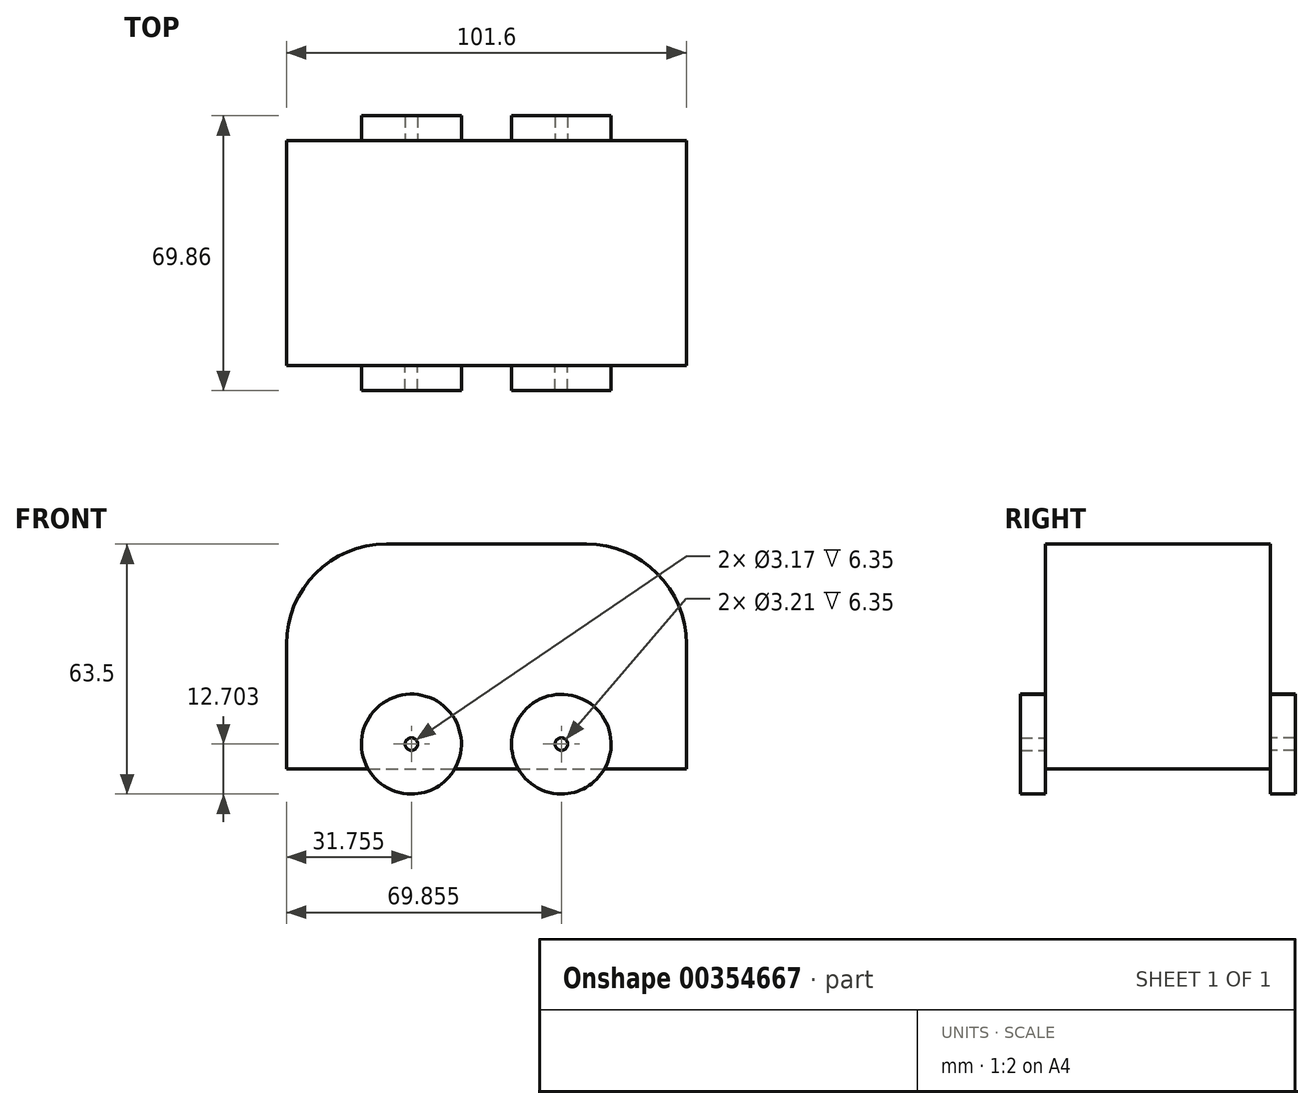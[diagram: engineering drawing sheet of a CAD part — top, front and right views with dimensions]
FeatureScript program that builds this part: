
annotation { "Feature Type Name" : "Feature", "Feature Type Description" : "" }
export const myFeature = defineFeature(function(context is Context, id is Id, definition is map)
    precondition{}
    {
        {
            var Q0;
            Q0=qCreatedBy(makeId("Front.planeOp"),FACE);
            var sketch = newSketch(context, id + "F0", { "sketchPlane" : qUnion([Q0])});
            skLineSegment(sketch, "E0.bottom", {"start": v(-26.04, 40.52) * mm, "end": v(24.77, 40.52) * mm});
            skLineSegment(sketch, "E0.top", {"start": v(-51.44, -16.63) * mm, "end": v(50.16, -16.63) * mm});
            skLineSegment(sketch, "E0.left", {"start": v(-51.44, 15.12) * mm, "end": v(-51.44, -16.63) * mm});
            skLineSegment(sketch, "E0.right", {"start": v(50.16, 15.12) * mm, "end": v(50.16, -16.63) * mm});
            skPoint(sketch, "E1.visualSharp", {"position": v(-51.44, 40.52) * mm});
            skArc(sketch, "E1.filletArc", {"start": v(-26.04, 40.52) * mm, "mid": v(-44, 33.08) * mm, "end": v(-51.44, 15.12) * mm});
            skPoint(sketch, "E2.visualSharp", {"position": v(50.16, 40.52) * mm});
            skArc(sketch, "E2.filletArc", {"start": v(50.16, 15.12) * mm, "mid": v(42.73, 33.08) * mm, "end": v(24.77, 40.52) * mm});
            skSolve(sketch);
        }
        {
            var Q0;
            Q0 = qSketchRegion(id + "F0", true);
            extrude(context, id + "F1", {"entities" : qUnion([Q0]), "endBound" : BoundingType.SYMMETRIC, "depth" : 57.15 * mm});
        }
        {
            var Q0;
            Q0=makeQuery(id+"F1.opExtrude","CAP_FACE",FACE,{"disambiguationData":[OSD([sQuery(id+"F0.wireOp",EDGE,"E0.bottom"),sQuery(id+"F0.wireOp",EDGE,"E0.top"),sQuery(id+"F0.wireOp",EDGE,"E0.left"),sQuery(id+"F0.wireOp",EDGE,"E0.right")])],"isStart":false});
            var sketch = newSketch(context, id + "F2", { "sketchPlane" : qUnion([Q0])});
            skCircle(sketch, "E3", {"center": v(-19.69, -10.28) * mm, "radius": 12.7 * mm});
            skCircle(sketch, "E4", {"center": v(18.41, -10.28) * mm, "radius": 12.7 * mm});
            skCircle(sketch, "E5", {"center": v(-19.69, -10.28) * mm, "radius": 13 * mm});
            skCircle(sketch, "E6", {"center": v(18.41, -10.28) * mm, "radius": 12.66 * mm});
            skCircle(sketch, "E7", {"center": v(-19.69, -10.28) * mm, "radius": 13.03 * mm});
            skCircle(sketch, "E8", {"center": v(18.41, -10.28) * mm, "radius": 12.67 * mm});
            skCircle(sketch, "E9", {"center": v(18.41, -10.28) * mm, "radius": 1.59 * mm});
            skCircle(sketch, "E10", {"center": v(-19.69, -10.28) * mm, "radius": 1.59 * mm});
            skCircle(sketch, "E11", {"center": v(-19.69, -10.28) * mm, "radius": 12.96 * mm});
            skCircle(sketch, "E12", {"center": v(18.41, -10.28) * mm, "radius": 12.65 * mm});
            skCircle(sketch, "E13", {"center": v(-19.69, -10.28) * mm, "radius": 12.9 * mm});
            skCircle(sketch, "E14", {"center": v(18.41, -10.28) * mm, "radius": 12.72 * mm});
            skCircle(sketch, "E15", {"center": v(18.41, -10.28) * mm, "radius": 1.6 * mm});
            skCircle(sketch, "E16", {"center": v(-19.69, -10.28) * mm, "radius": 1.54 * mm});
            skCircle(sketch, "E17", {"center": v(18.41, -10.28) * mm, "radius": 12.8 * mm});
            skCircle(sketch, "E18", {"center": v(-19.69, -10.28) * mm, "radius": 12.95 * mm});
            skSolve(sketch);
        }
        {
            var Q0;
            Q0=makeQuery(id+"F2.imprint","IMPRINT",FACE,{"disambiguationData":[TD([[makeQuery(id+"F2.imprint","IMPRINT",EDGE,{"derivedFrom":sQuery(id+"F2.wireOp",EDGE,"E10")}),-1.0]])]});
            var Q1;
            {var subQ0=sQuery(id+"F2.wireOp",EDGE,"E3");var subQ1=makeQuery(id+"F1.opExtrude","CAP_EDGE",EDGE,{"disambiguationData":[OSD([sQuery(id+"F0.wireOp",EDGE,"E0.top")])],"isStart":false});var subQ2=makeQuery(id+"F2.imprint","INTERSECT",VERTEX,{"disambiguationData":[OD(0.0)],"derivedFrom":[subQ1,subQ0]});Q1=makeQuery(id+"F2.imprint","IMPRINT",FACE,{"disambiguationData":[TD([[makeQuery(id+"F2.imprint","IMPRINT",EDGE,{"disambiguationData":[TD([[subQ2,-1.0]])],"derivedFrom":subQ0}),1.0]])]});}
            var Q2;
            {var subQ0=sQuery(id+"F2.wireOp",EDGE,"E12");var subQ1=makeQuery(id+"F1.opExtrude","CAP_EDGE",EDGE,{"disambiguationData":[OSD([sQuery(id+"F0.wireOp",EDGE,"E0.top")])],"isStart":false});var subQ2=makeQuery(id+"F2.imprint","INTERSECT",VERTEX,{"disambiguationData":[OD(0.0)],"derivedFrom":[subQ1,subQ0]});Q2=makeQuery(id+"F2.imprint","IMPRINT",FACE,{"disambiguationData":[TD([[makeQuery(id+"F2.imprint","IMPRINT",EDGE,{"disambiguationData":[TD([[subQ2,1.0]])],"derivedFrom":subQ0}),1.0]])]});}
            var Q3;
            Q3=makeQuery(id+"F2.imprint","IMPRINT",FACE,{"disambiguationData":[TD([[makeQuery(id+"F2.imprint","IMPRINT",EDGE,{"derivedFrom":sQuery(id+"F2.wireOp",EDGE,"E15")}),-1.0]])]});
            extrude(context, id + "F3", {"entities" : qUnion([Q0, Q1, Q2, Q3]), "depth" : 6.35 * mm});
        }
        {
            var Q0;
            Q0=makeQuery(id+"F3.opExtrude","SWEPT_BODY",BODY,{"disambiguationData":[OSD([sQuery(id+"F2.wireOp",EDGE,"E3"),sQuery(id+"F2.wireOp",EDGE,"E10")])]});
            var Q1;
            Q1=makeQuery(id+"F3.opExtrude","SWEPT_BODY",BODY,{"disambiguationData":[OSD([sQuery(id+"F2.wireOp",EDGE,"E12"),sQuery(id+"F2.wireOp",EDGE,"E15")])]});
            var Q2;
            Q2=qCreatedBy(makeId("Front.planeOp"),FACE);
            mirror(context, id + "F4", {"operationType" : NewBodyOperationType.ADD, "entities" : qUnion([Q0, Q1]), "mirrorPlane" : qUnion([Q2])});
        }
    });
